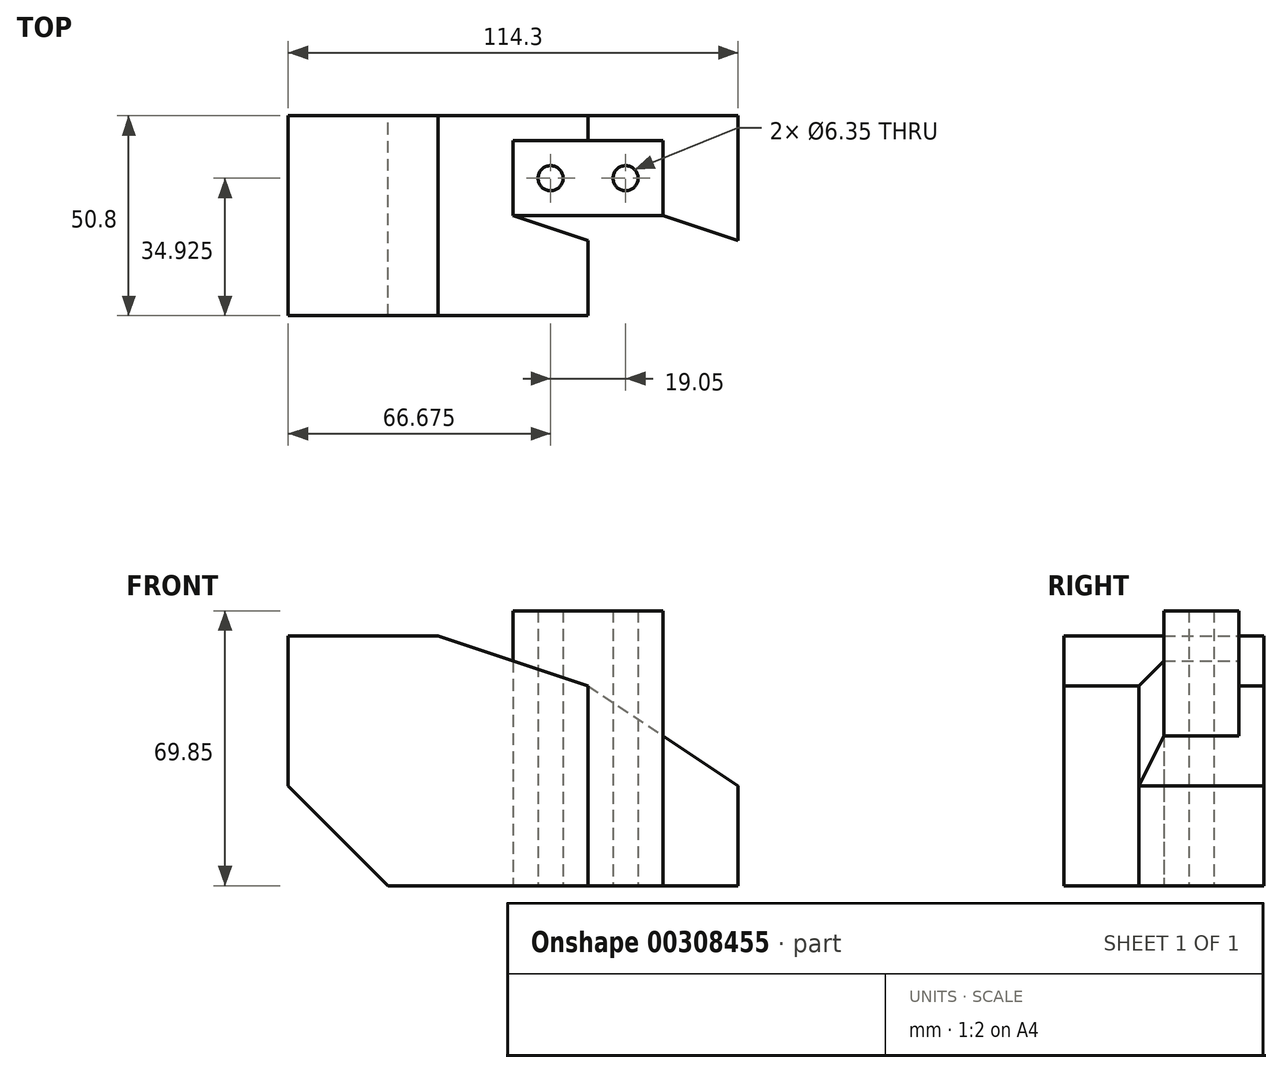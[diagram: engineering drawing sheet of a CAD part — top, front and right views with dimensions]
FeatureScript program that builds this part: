
annotation { "Feature Type Name" : "Feature", "Feature Type Description" : "" }
export const myFeature = defineFeature(function(context is Context, id is Id, definition is map)
    precondition{}
    {
        {
            var Q0;
            Q0=qCreatedBy(makeId("Front.planeOp"),FACE);
            var sketch = newSketch(context, id + "F0", { "sketchPlane" : qUnion([Q0])});
            skLineSegment(sketch, "E0", {"start": v(0, 0) * mm, "end": v(88.9, 0) * mm});
            skLineSegment(sketch, "E1", {"start": v(88.9, 0) * mm, "end": v(88.9, 25.4) * mm});
            skLineSegment(sketch, "E2", {"start": v(12.7, 63.5) * mm, "end": v(-25.4, 63.5) * mm});
            skLineSegment(sketch, "E3", {"start": v(-25.4, 63.5) * mm, "end": v(-25.4, 25.4) * mm});
            skLineSegment(sketch, "E4", {"start": v(-25.4, 25.4) * mm, "end": v(0, 0) * mm});
            skLineSegment(sketch, "E5", {"start": v(12.7, 63.5) * mm, "end": v(50.8, 50.8) * mm});
            skLineSegment(sketch, "E6", {"start": v(88.9, 25.4) * mm, "end": v(50.8, 50.8) * mm});
            skSolve(sketch);
        }
        {
            var Q0;
            Q0 = qSketchRegion(id + "F0", true);
            extrude(context, id + "F1", {"entities" : qUnion([Q0]), "endBound" : BoundingType.SYMMETRIC, "depth" : 50.8 * mm});
        }
        {
            var Q0;
            Q0=qCreatedBy(makeId("Top.planeOp"),FACE);
            var sketch = newSketch(context, id + "F2", { "sketchPlane" : qUnion([Q0])});
            skLineSegment(sketch, "E7.bottom", {"start": v(50.8, -25.4) * mm, "end": v(88.9, -25.4) * mm});
            skLineSegment(sketch, "E7.top", {"start": v(50.8, -6.35) * mm, "end": v(88.9, -6.35) * mm});
            skLineSegment(sketch, "E7.left", {"start": v(50.8, -25.4) * mm, "end": v(50.8, -6.35) * mm});
            skLineSegment(sketch, "E7.right", {"start": v(88.9, -25.4) * mm, "end": v(88.9, -6.35) * mm});
            skSolve(sketch);
        }
        {
            var Q0;
            Q0 = qSketchRegion(id + "F2", true);
            extrude(context, id + "F3", {"entities" : qUnion([Q0]), "operationType" : NewBodyOperationType.REMOVE, "endBound" : BoundingType.THROUGH_ALL, "depth" : 25.4 * mm});
        }
        {
            var Q0;
            Q0=qCreatedBy(makeId("Top.planeOp"),FACE);
            var sketch = newSketch(context, id + "F4", { "sketchPlane" : qUnion([Q0])});
            skLineSegment(sketch, "E8.bottom", {"start": v(31.75, 19.05) * mm, "end": v(69.85, 19.05) * mm});
            skLineSegment(sketch, "E8.top", {"start": v(31.75, 0) * mm, "end": v(69.85, 0) * mm});
            skLineSegment(sketch, "E8.left", {"start": v(31.75, 19.05) * mm, "end": v(31.75, 0) * mm});
            skLineSegment(sketch, "E8.right", {"start": v(69.85, 19.05) * mm, "end": v(69.85, 0) * mm});
            skCircle(sketch, "E9", {"center": v(41.28, 9.52) * mm, "radius": 3.18 * mm});
            skCircle(sketch, "E10", {"center": v(60.33, 9.52) * mm, "radius": 3.18 * mm});
            skSolve(sketch);
        }
        {
            var Q0;
            Q0 = qSketchRegion(id + "F4", true);
            extrude(context, id + "F5", {"entities" : qUnion([Q0]), "operationType" : NewBodyOperationType.ADD, "depth" : 69.85 * mm});
        }
        {
            var Q0;
            Q0=makeQuery(id+"F5.opExtrude","CAP_FACE",FACE,{"disambiguationData":[OSD([sQuery(id+"F4.wireOp",EDGE,"E8.bottom"),sQuery(id+"F4.wireOp",EDGE,"E8.top"),sQuery(id+"F4.wireOp",EDGE,"E8.left"),sQuery(id+"F4.wireOp",EDGE,"E8.right"),sQuery(id+"F4.wireOp",EDGE,"E9"),sQuery(id+"F4.wireOp",EDGE,"E10")])],"isStart":false});
            var sketch = newSketch(context, id + "F6", { "sketchPlane" : qUnion([Q0])});
            skCircle(sketch, "E11", {"center": v(60.33, 9.52) * mm, "radius": 3.18 * mm});
            skCircle(sketch, "E12", {"center": v(41.28, 9.52) * mm, "radius": 3.18 * mm});
            skSolve(sketch);
        }
        {
            var Q0;
            Q0 = qSketchRegion(id + "F6", true);
            extrude(context, id + "F7", {"entities" : qUnion([Q0]), "operationType" : NewBodyOperationType.REMOVE, "endBound" : BoundingType.THROUGH_ALL, "oppositeDirection" : true, "depth" : 25.4 * mm});
        }
        {
            var Q0;
            Q0=qCreatedBy(makeId("Top.planeOp"),FACE);
            var sketch = newSketch(context, id + "F8", { "sketchPlane" : qUnion([Q0])});
            skLineSegment(sketch, "E13", {"start": v(31.75, 0) * mm, "end": v(69.85, 0) * mm});
            skLineSegment(sketch, "E14", {"start": v(69.85, 0) * mm, "end": v(88.9, -6.35) * mm});
            skLineSegment(sketch, "E15", {"start": v(88.9, -6.35) * mm, "end": v(50.8, -6.35) * mm});
            skLineSegment(sketch, "E16", {"start": v(50.8, -6.35) * mm, "end": v(31.75, 0) * mm});
            skSolve(sketch);
        }
        {
            var Q0;
            Q0 = qSketchRegion(id + "F8", true);
            extrude(context, id + "F9", {"entities" : qUnion([Q0]), "operationType" : NewBodyOperationType.REMOVE, "endBound" : BoundingType.THROUGH_ALL, "depth" : 25.4 * mm});
        }
    });
